# Revit family: Ceiling Batt (R6.0)
name_source: partatom
category: Generic Models
units: mm (PartAtom-declared; Revit-internal decimal feet)

## family parameters
Can host rebar = No
Cut with Voids When Loaded = No
Host = Face
Part Type = Normal
Room Calculation Point = No
Round Connector Dimension = Use Diameter
Shared = No

## types (1)
- R6.0 - Ceiling Batts
    Default Elevation = 1219 mm
    Density = 9.00 kg/m³
    Description = Ecowool Wall Acoustic Batts is semi-rigid or rigid slabs of non-combustible, water repellent, glass mineral wool. They are designed to suit internal walls and ceiling of residential, commercial and industrial buildings. Excellent thermal, acoustic and fire safety performance
    Finish = Ceiling Batt
    Insulation Thickness = 278 mm  [stored 0.912073 ft]
    Manufacturer = PGF Insulation Sdn. Bhd.
    Thermal K value = 0.0396
    Thermal R value = 6
    Type of Insulation = Glass Mineral Wool Blanket with vapour barrier
    URL = www.ecowool.com.au

note: [stored X ft] marks values corroborated as IEEE doubles in the binary element streams (Revit-internal decimal feet)

## geometry (parser evidence)
native form markers: Sweep x2
no freeform markers — native parametric forms only
